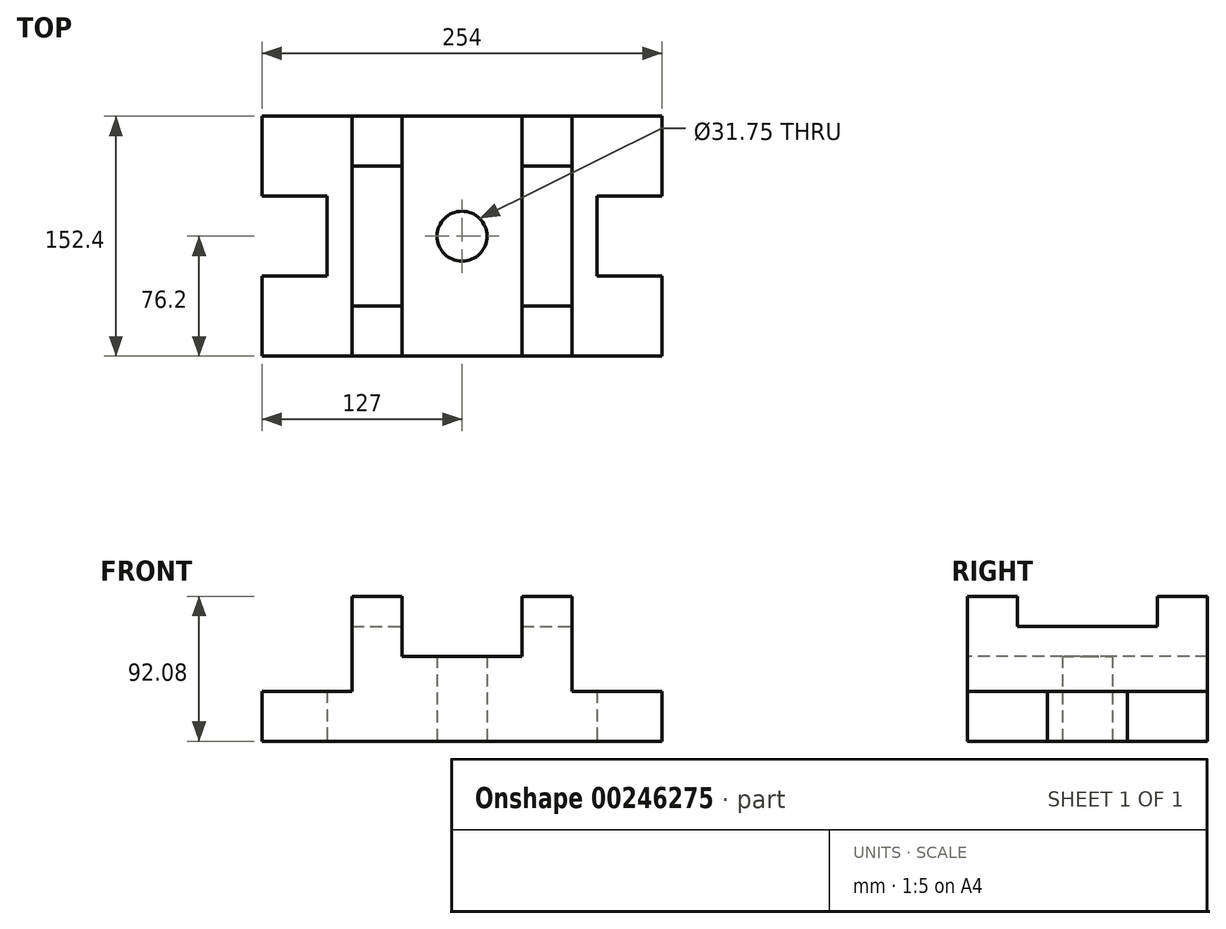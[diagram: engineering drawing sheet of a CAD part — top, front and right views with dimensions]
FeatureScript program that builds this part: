
annotation { "Feature Type Name" : "Feature", "Feature Type Description" : "" }
export const myFeature = defineFeature(function(context is Context, id is Id, definition is map)
    precondition{}
    {
        {
            var Q0;
            Q0=qCreatedBy(makeId("Top.planeOp"),FACE);
            var sketch = newSketch(context, id + "F0", { "sketchPlane" : qUnion([Q0])});
            skLineSegment(sketch, "E0.bottom", {"start": v(0, 0) * mm, "end": v(254, 0) * mm});
            skLineSegment(sketch, "E0.top", {"start": v(0, 152.4) * mm, "end": v(254, 152.4) * mm});
            skLineSegment(sketch, "E0.left", {"start": v(0, 0) * mm, "end": v(0, 152.4) * mm});
            skLineSegment(sketch, "E0.right", {"start": v(254, 0) * mm, "end": v(254, 152.4) * mm});
            skLineSegment(sketch, "E1.bottom", {"start": v(0, 101.6) * mm, "end": v(41.27, 101.6) * mm});
            skLineSegment(sketch, "E1.top", {"start": v(0, 50.8) * mm, "end": v(41.27, 50.8) * mm});
            skLineSegment(sketch, "E1.left", {"start": v(0, 101.6) * mm, "end": v(0, 50.8) * mm});
            skLineSegment(sketch, "E1.right", {"start": v(41.27, 101.6) * mm, "end": v(41.27, 50.8) * mm});
            skLineSegment(sketch, "E2.bottom", {"start": v(254, 101.6) * mm, "end": v(212.72, 101.6) * mm});
            skLineSegment(sketch, "E2.top", {"start": v(254, 50.8) * mm, "end": v(212.72, 50.8) * mm});
            skLineSegment(sketch, "E2.left", {"start": v(254, 101.6) * mm, "end": v(254, 50.8) * mm});
            skLineSegment(sketch, "E2.right", {"start": v(212.72, 101.6) * mm, "end": v(212.72, 50.8) * mm});
            skCircle(sketch, "E3", {"center": v(127, 76.2) * mm, "radius": 15.88 * mm});
            skSolve(sketch);
        }
        {
            var Q0;
            {var subQ1=sQuery(id+"F0.wireOp",EDGE,"E0.bottom");Q0=makeQuery(id+"F0.imprint","IMPRINT",FACE,{"disambiguationData":[TD([[makeQuery(id+"F0.imprint","IMPRINT",EDGE,{"derivedFrom":subQ1}),1.0]])]});}
            extrude(context, id + "F1", {"entities" : qUnion([Q0]), "depth" : 31.75 * mm});
        }
        {
            var Q0;
            Q0=makeQuery(id+"F1.opExtrude","SWEPT_FACE",FACE,{"disambiguationData":[OSD([sQuery(id+"F0.wireOp",EDGE,"E0.bottom")])]});
            var sketch = newSketch(context, id + "F2", { "sketchPlane" : qUnion([Q0])});
            skLineSegment(sketch, "E4.bottom", {"start": v(57.15, 31.75) * mm, "end": v(196.85, 31.75) * mm});
            skLineSegment(sketch, "E4.top", {"start": v(57.15, 92.08) * mm, "end": v(196.85, 92.08) * mm});
            skLineSegment(sketch, "E4.left", {"start": v(57.15, 31.75) * mm, "end": v(57.15, 92.08) * mm});
            skLineSegment(sketch, "E4.right", {"start": v(196.85, 31.75) * mm, "end": v(196.85, 92.08) * mm});
            skLineSegment(sketch, "E5.bottom", {"start": v(88.9, 92.08) * mm, "end": v(165.1, 92.08) * mm});
            skLineSegment(sketch, "E5.top", {"start": v(88.9, 53.97) * mm, "end": v(165.1, 53.98) * mm});
            skLineSegment(sketch, "E5.left", {"start": v(88.9, 92.08) * mm, "end": v(88.9, 53.97) * mm});
            skLineSegment(sketch, "E5.right", {"start": v(165.1, 92.08) * mm, "end": v(165.1, 53.98) * mm});
            skSolve(sketch);
        }
        {
            var Q0;
            Q0=makeQuery(id+"F2.imprint","IMPRINT",FACE,{"disambiguationData":[TD([[makeQuery(id+"F2.imprint","IMPRINT",EDGE,{"derivedFrom":sQuery(id+"F2.wireOp",EDGE,"E4.bottom")}),1.0]])]});
            var Q1;
            Q1=makeQuery(id+"F1.opExtrude","SWEPT_FACE",FACE,{"disambiguationData":[OSD([sQuery(id+"F0.wireOp",EDGE,"E0.top")])]});
            extrude(context, id + "F3", {"entities" : qUnion([Q0]), "operationType" : NewBodyOperationType.ADD, "endBound" : BoundingType.UP_TO_SURFACE, "oppositeDirection" : true, "endBoundEntityFace" : qUnion([Q1]), "depth" : 25.4 * mm});
        }
        {
            var Q0;
            Q0=makeQuery(id+"F3.opExtrude","SWEPT_FACE",FACE,{"disambiguationData":[OSD([sQuery(id+"F2.wireOp",EDGE,"E4.right")])]});
            var sketch = newSketch(context, id + "F4", { "sketchPlane" : qUnion([Q0])});
            skLineSegment(sketch, "E6.bottom", {"start": v(31.75, 92.07) * mm, "end": v(120.65, 92.07) * mm});
            skLineSegment(sketch, "E6.top", {"start": v(31.75, 73.02) * mm, "end": v(120.65, 73.02) * mm});
            skLineSegment(sketch, "E6.left", {"start": v(31.75, 92.07) * mm, "end": v(31.75, 73.02) * mm});
            skLineSegment(sketch, "E6.right", {"start": v(120.65, 92.07) * mm, "end": v(120.65, 73.02) * mm});
            skSolve(sketch);
        }
        {
            var Q0;
            Q0=makeQuery(id+"F4.imprint","IMPRINT",FACE,{"disambiguationData":[TD([[makeQuery(id+"F4.imprint","IMPRINT",EDGE,{"derivedFrom":sQuery(id+"F4.wireOp",EDGE,"E6.bottom")}),1.0]])]});
            extrude(context, id + "F5", {"entities" : qUnion([Q0]), "operationType" : NewBodyOperationType.REMOVE, "oppositeDirection" : true, "depth" : 254 * mm});
        }
        {
            var Q0;
            Q0=makeQuery(id+"F0.imprint","IMPRINT",FACE,{"disambiguationData":[TD([[makeQuery(id+"F0.imprint","IMPRINT",EDGE,{"derivedFrom":sQuery(id+"F0.wireOp",EDGE,"E3")}),1.0]])]});
            extrude(context, id + "F6", {"entities" : qUnion([Q0]), "operationType" : NewBodyOperationType.REMOVE, "endBound" : BoundingType.THROUGH_ALL, "depth" : 25.4 * mm});
        }
    });
